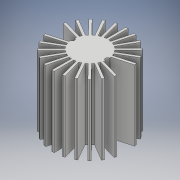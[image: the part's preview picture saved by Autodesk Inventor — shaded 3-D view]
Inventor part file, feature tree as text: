
AUTODESK INVENTOR PART (.ipt)
format: ipt  version: 2018 (Build 220112000, 112)  size: 283,136 bytes
history: native  units: mm
features: extrude x3, sketch x3
ambient origin geometry x8: Origin, YZ Plane, XZ Plane, XY Plane, X Axis, Y Axis, Z Axis, Center Point
bodies: Solid1 (feature_tree)
feature tree (6):
  extrude  "Extrusion1"  Depth=40.0mm TaperAngle=0.0deg
  extrude  "Extrusion2"  Depth=2.43mm
  extrude  "Extrusion3"  Depth=40.0mm
  sketch  "Sketch1"  dims[d0=19.91mm d1=40.0mm d2=0.0mm]
  sketch  "Sketch2"  dims[d3=2.43mm d4=2.43mm]
  sketch  "Sketch3"  dims[d5=40.0mm d6=0.0mm d7=42.0116mm d8=11.44mm d9=11.44mm d10=0.65mm d11=0.65mm d12=40.0mm d13=0.0mm d14=110.0mm d16=25.900686mm d18=0.65mm d19=0.65mm d20=110.0mm d22=25.900686mm]
